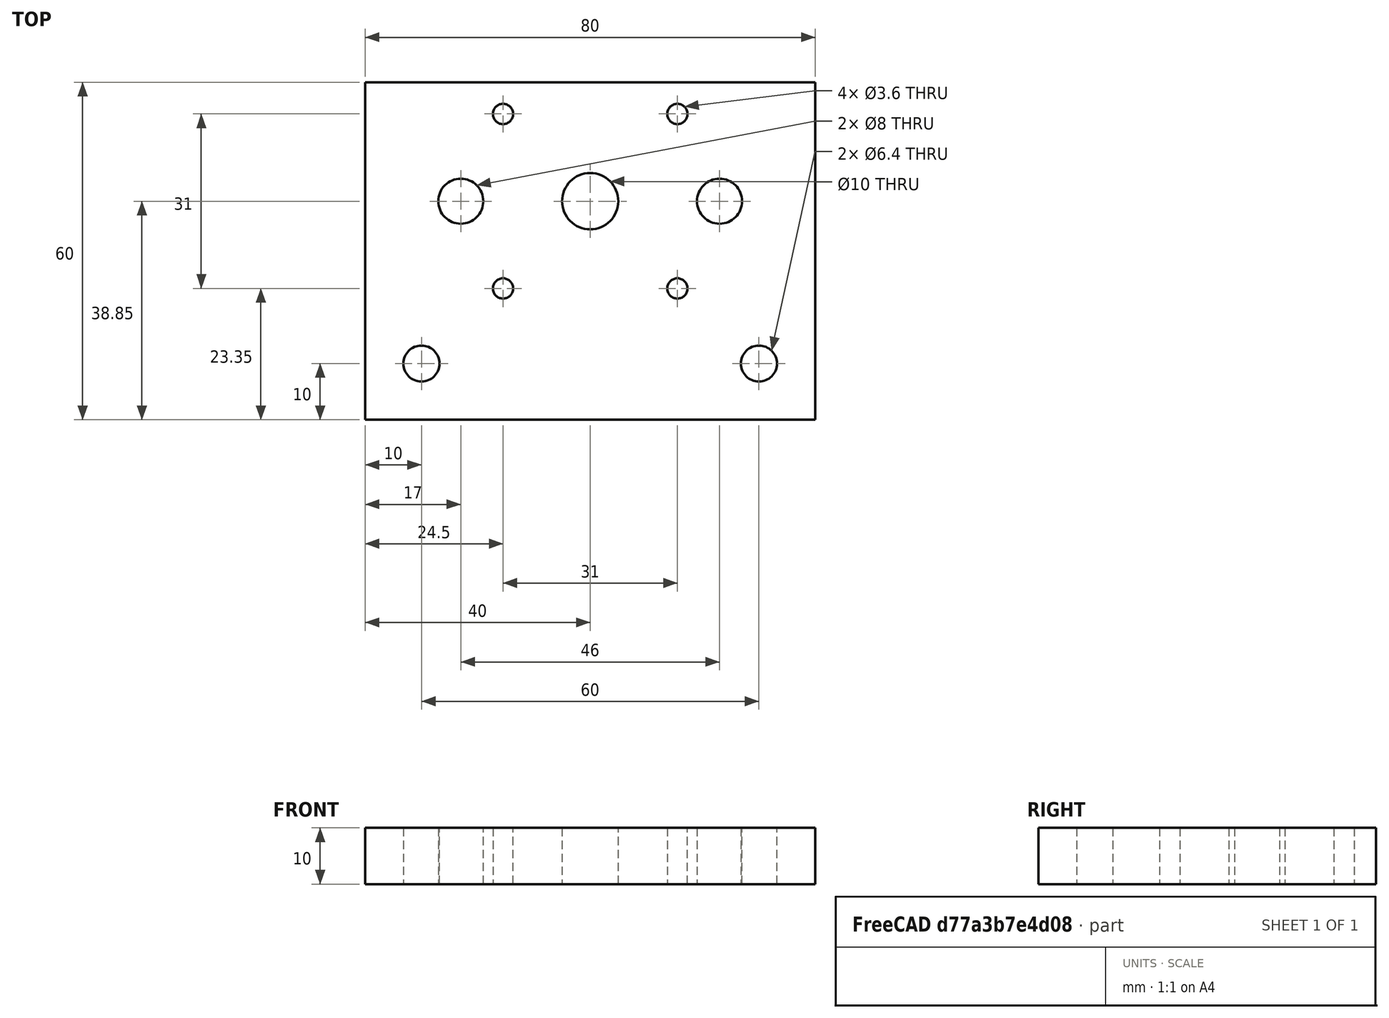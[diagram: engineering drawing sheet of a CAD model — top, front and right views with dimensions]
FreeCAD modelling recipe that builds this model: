
FCSTD DOCUMENT  (FreeCAD 0.18R16110 (Git))
Label: mountplate2a
License: All rights reserved
LicenseURL: http://en.wikipedia.org/wiki/All_rights_reserved
objects: Sketcher::SketchObject×1, PartDesign::Pad×1, PartDesign::Body×1
note: 4 computed .brp shape members not serialized (recipe doc carries the construction recipe); baked Part::Feature solids carry a one-line shape summary decoded from their .brp

FEATURE [Sketcher::SketchObject] Sketch
  MapMode = 5
  Support = -> [XY_Plane]
  sketch-geometry (13):
    g0: LineSegment StartX=0 StartY=60 StartZ=0 EndX=80 EndY=60 EndZ=0
    g1: LineSegment StartX=80 StartY=60 StartZ=0 EndX=80 EndY=0 EndZ=0
    g2: LineSegment StartX=80 StartY=0 StartZ=0 EndX=0 EndY=0 EndZ=0
    g3: LineSegment StartX=0 StartY=0 StartZ=0 EndX=0 EndY=60 EndZ=0
    g4: Circle CenterX=40 CenterY=38.85 CenterZ=0 NormalX=0 NormalY=0 NormalZ=1 AngleXU=0 Radius=5
    g5: Circle CenterX=55.5 CenterY=54.35 CenterZ=0 NormalX=0 NormalY=0 NormalZ=1 AngleXU=0 Radius=1.8
    g6: Circle CenterX=55.5 CenterY=23.35 CenterZ=0 NormalX=0 NormalY=0 NormalZ=1 AngleXU=0 Radius=1.8
    g7: Circle CenterX=24.5 CenterY=23.35 CenterZ=0 NormalX=0 NormalY=0 NormalZ=1 AngleXU=0 Radius=1.8
    g8: Circle CenterX=24.5 CenterY=54.35 CenterZ=0 NormalX=0 NormalY=0 NormalZ=1 AngleXU=0 Radius=1.8
    g9: Circle CenterX=10 CenterY=10 CenterZ=0 NormalX=0 NormalY=0 NormalZ=1 AngleXU=0 Radius=3.2
    g10: Circle CenterX=70 CenterY=10 CenterZ=0 NormalX=0 NormalY=0 NormalZ=1 AngleXU=0 Radius=3.2
    g11: Circle CenterX=63 CenterY=38.85 CenterZ=0 NormalX=0 NormalY=0 NormalZ=1 AngleXU=0 Radius=4
    g12: Circle CenterX=17 CenterY=38.85 CenterZ=0 NormalX=0 NormalY=0 NormalZ=1 AngleXU=0 Radius=4
  constraints (38):
    c: Coincident(g0,g1)
    c: Coincident(g1,g2)
    c: Coincident(g2,g3)
    c: Coincident(g3,g0)
    c: Horizontal(g0)
    c: Horizontal(g2)
    c: Vertical(g1)
    c: Vertical(g3)
    c: Coincident(g2,g-1)
    c: DistanceY(g3,g3) = 60
    c: DistanceX(g2,g2) = 80
    c: DistanceX(g2,g4) = 40
    c: DistanceY(g2,g4) = 38.85
    c: Radius(g4) = 5
    c: DistanceY(g4,g5) = 15.5
    c: DistanceX(g6,g5) = 0
    c: DistanceX(g4,g5) = 15.5
    c: DistanceY(g8,g5) = 0
    c: DistanceX(g8,g5) = 31
    c: DistanceX(g7,g8) = 0
    c: DistanceY(g6,g5) = 31
    c: DistanceY(g6,g7) = 0
    c: Radius(g8) = 1.8
    c: Equal(g8,g5)
    c: Equal(g8,g6)
    c: Equal(g8,g7)
    c: DistanceX(g2,g9) = 10
    c: DistanceY(g2,g9) = 10
    c: DistanceY(g9,g10) = 0
    c: DistanceX(g10,g1) = 10
    c: DistanceY(g11,g12) = 0
    c: DistanceX(g11,g0) = 17
    c: DistanceY(g12,g0) = 21.15
    c: Radius(g9) = 3.2
    c: Equal(g9,g10)
    c: Radius(g12) = 4
    c: Equal(g12,g11)
    c: DistanceX(g2,g12) = 17
FEATURE [PartDesign::Pad] Pad
  Length = 10
  Length2 = 100
  Profile = -> Sketch
  Type = 0
FEATURE [PartDesign::Body] Body
  Group = -> [Sketch,Pad]
  Origin = -> Origin
  Tip = -> Pad
